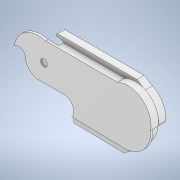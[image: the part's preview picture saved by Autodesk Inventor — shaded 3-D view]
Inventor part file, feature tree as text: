
AUTODESK INVENTOR PART (.ipt)
format: ipt  version: 2022 (Build 260153000, 153)  size: 207,872 bytes
history: native  units: in
note: dims shown in document units (in); Inventor stores cm internally (conversion verified against a paired STEP export)
features: extrude x5, sketch x5, other x1
ambient origin geometry x8: Origin, YZ Plane, XZ Plane, XY Plane, X Axis, Y Axis, Z Axis, Center Point
bodies: Body1 (feature_tree)
feature tree (11):
  other  "Sólido1"
  extrude  "Extrusión1"  Depth=0.0315in TaperAngle=0.0deg
  extrude  "Extrusión2"  Depth=0.1024in TaperAngle=0.0deg
  extrude  "Extrusión3"  Depth=0.0157in TaperAngle=0.0deg
  extrude  "Extrusión4"  Depth=0.0197in
  extrude  "Extrusión5"  [1 undecoded]
  sketch  "Boceto1"  dims[d4=0.2441in d5=0.0315in d6=0.0in]
  sketch  "Boceto2"  dims[d7=0.0709in d8=0.0in d9=0.1024in d10=0.0in]
  sketch  "Boceto3"  dims[d11=0.0394in d12=0.0in d13=0.0157in d14=0.0in]
  sketch  "Boceto4"  dims[d15=0.0787in d16=0.0197in]
  sketch  "Boceto5"
note: 1 required parameter value undecoded (feature->parameter linkage not recoverable at this tier; creation-order binding heuristic only, values carry confidence <= 0.55)
